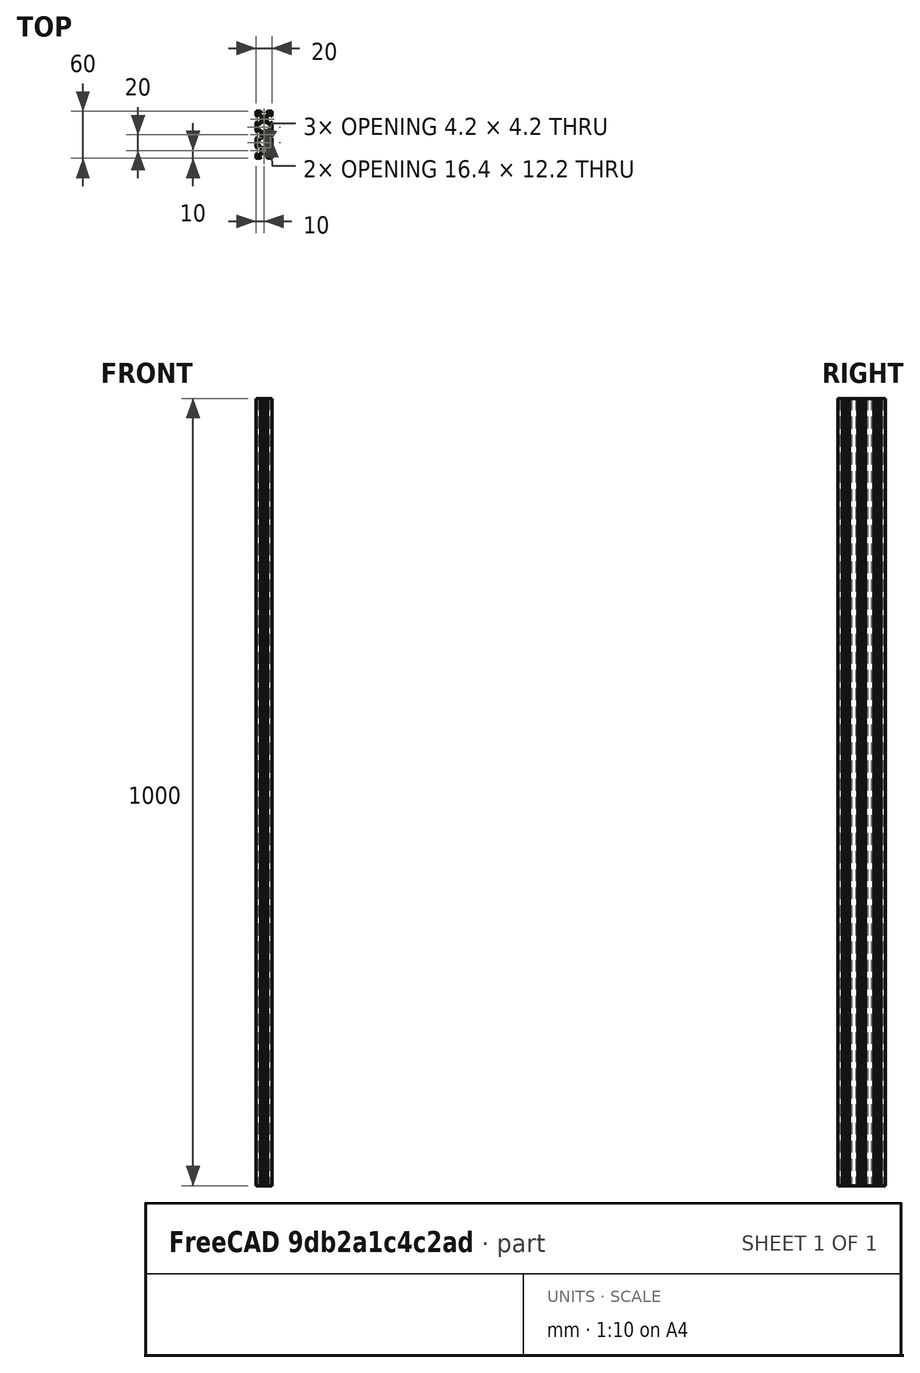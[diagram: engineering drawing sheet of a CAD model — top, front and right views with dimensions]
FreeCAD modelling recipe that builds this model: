
FCSTD DOCUMENT  (FreeCAD 2022.430R26244 +4758 (Git))
Label: as3V-Slot 20x60x1000 Linear Rail
License: All rights reserved
LicenseURL: http://en.wikipedia.org/wiki/All_rights_reserved
objects: Part::FeaturePython×7, App::FeaturePython×2, Part::Feature×1
note: 7 computed .brp shape members not serialized (recipe doc carries the construction recipe); baked Part::Feature solids carry a one-line shape summary decoded from their .brp

FEATURE [Part::Feature] Solid  label="V-Slot 20x60x1000 Linear Rail"
  TreeRank = 0
  shape: bbox 20 x 60 x 1000 mm, 160 faces (baked)
FEATURE [App::FeaturePython] Constraints  # WARN: FeaturePython — macro-defined, semantics opaque (R4)
  TreeRank = 0
  _LinkVersion = 1
  _Version = 1
FEATURE [Part::FeaturePython] Parts  # WARN: FeaturePython — macro-defined, semantics opaque (R4)
  Group = -> [Solid]
  GroupMode = 0
  TreeRank = 0
  _LinkVersion = 1
FEATURE [Part::FeaturePython] Assembly  label="As3V-Slot 20x60x1000 Linear Rail"  # WARN: FeaturePython — macro-defined, semantics opaque (R4)
  AutoRelax = true
  BuildShape = 0
  Freeze = false
  Group = -> [Constraints,Elements,Parts]
  TreeRank = 0
  Verbose = false
  _LinkVersion = 1
  _SolverType = 1
  _Version = 1
FEATURE [App::FeaturePython] Elements  # WARN: FeaturePython — macro-defined, semantics opaque (R4)
  Group = -> [Element,Element001,Element002,Element003,Element004]
  TreeRank = 0
  _LinkVersion = 1
FEATURE [Part::FeaturePython] Element  label="FaceVref"  # link proxy (typed FeaturePython)
  Detach = false
  LinkTransform = true
  LinkedObject = -> Solid [Face61]
  TreeRank = 0
  _LinkVersion = 1
  _Parent = -> Elements
FEATURE [Part::FeaturePython] Element001  label="FaceLat"  # link proxy (typed FeaturePython)
  Detach = false
  LinkTransform = true
  LinkedObject = -> Solid [Face78]
  TreeRank = 0
  _LinkVersion = 1
  _Parent = -> Elements
FEATURE [Part::FeaturePython] Element002  label="Extrem1"  # link proxy (typed FeaturePython)
  Detach = false
  LinkTransform = true
  LinkedObject = -> Solid [Face160]
  TreeRank = 0
  _LinkVersion = 1
  _Parent = -> Elements
FEATURE [Part::FeaturePython] Element003  label="Extrem2"  # link proxy (typed FeaturePython)
  Detach = false
  LinkTransform = true
  LinkedObject = -> Solid [Face159]
  TreeRank = 0
  _LinkVersion = 1
  _Parent = -> Elements
FEATURE [Part::FeaturePython] Element004  label="FaceVref2"  # link proxy (typed FeaturePython)
  Detach = false
  LinkTransform = true
  LinkedObject = -> Solid [Face110]
  TreeRank = 0
  _LinkVersion = 1
  _Parent = -> Elements
